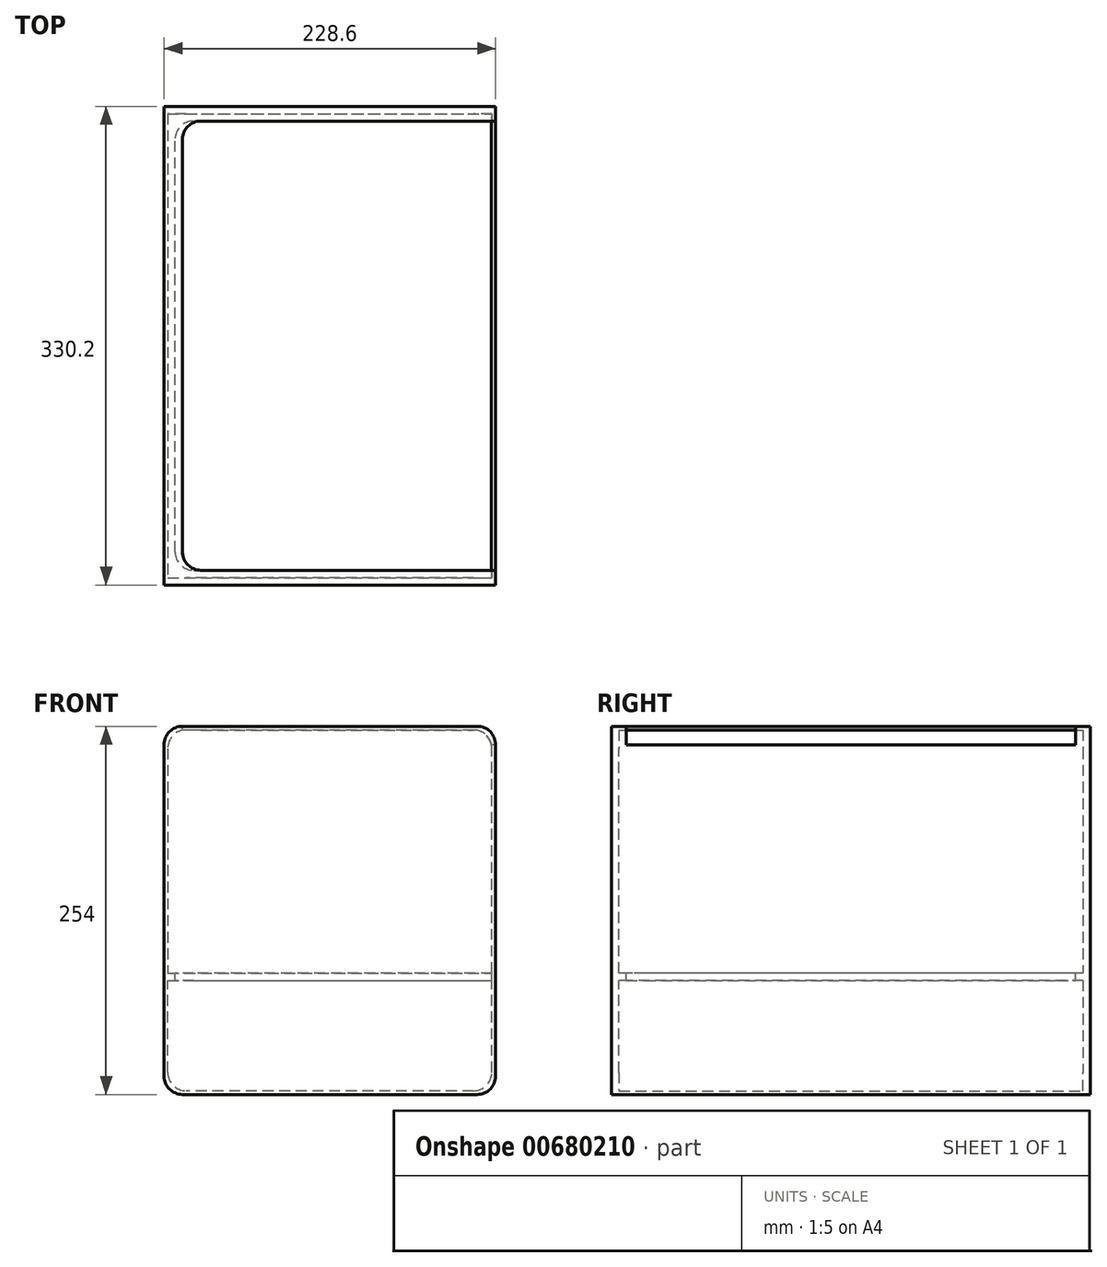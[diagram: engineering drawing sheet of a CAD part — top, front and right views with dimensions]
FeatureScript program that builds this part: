
annotation { "Feature Type Name" : "Feature", "Feature Type Description" : "" }
export const myFeature = defineFeature(function(context is Context, id is Id, definition is map)
    precondition{}
    {
        {
            var Q0;
            Q0=qCreatedBy(makeId("Front.planeOp"),FACE);
            var sketch = newSketch(context, id + "F0", { "sketchPlane" : qUnion([Q0])});
            skLineSegment(sketch, "E0.bottom", {"start": v(101.6, -127) * mm, "end": v(-101.6, -127) * mm});
            skLineSegment(sketch, "E0.top", {"start": v(101.6, 127) * mm, "end": v(-101.6, 127) * mm});
            skLineSegment(sketch, "E0.left", {"start": v(114.3, -114.3) * mm, "end": v(114.3, 114.3) * mm});
            skLineSegment(sketch, "E0.right", {"start": v(-114.3, -114.3) * mm, "end": v(-114.3, 114.3) * mm});
            skPoint(sketch, "E0.middle", {"position": v(0, 0) * mm});
            skPoint(sketch, "E1.visualSharp", {"position": v(114.3, 127) * mm});
            skArc(sketch, "E1.filletArc", {"start": v(114.3, 114.3) * mm, "mid": v(110.58, 123.28) * mm, "end": v(101.6, 127) * mm});
            skPoint(sketch, "E2.visualSharp", {"position": v(-114.3, 127) * mm});
            skArc(sketch, "E2.filletArc", {"start": v(-101.6, 127) * mm, "mid": v(-110.58, 123.28) * mm, "end": v(-114.3, 114.3) * mm});
            skPoint(sketch, "E3.visualSharp", {"position": v(-114.3, -127) * mm});
            skArc(sketch, "E3.filletArc", {"start": v(-114.3, -114.3) * mm, "mid": v(-110.58, -123.28) * mm, "end": v(-101.6, -127) * mm});
            skPoint(sketch, "E4.visualSharp", {"position": v(114.3, -127) * mm});
            skArc(sketch, "E4.filletArc", {"start": v(101.6, -127) * mm, "mid": v(110.58, -123.28) * mm, "end": v(114.3, -114.3) * mm});
            skLineSegment(sketch, "E5.bottom", {"start": v(99.06, -124.46) * mm, "end": v(-99.06, -124.46) * mm});
            skLineSegment(sketch, "E5.top", {"start": v(99.06, 124.46) * mm, "end": v(-99.06, 124.46) * mm});
            skLineSegment(sketch, "E5.left", {"start": v(111.76, -111.76) * mm, "end": v(111.76, 111.76) * mm});
            skLineSegment(sketch, "E5.right", {"start": v(-111.76, -111.76) * mm, "end": v(-111.76, 111.76) * mm});
            skPoint(sketch, "E6.visualSharp", {"position": v(-111.76, 124.46) * mm});
            skArc(sketch, "E6.filletArc", {"start": v(-99.06, 124.46) * mm, "mid": v(-108.04, 120.74) * mm, "end": v(-111.76, 111.76) * mm});
            skPoint(sketch, "E7.visualSharp", {"position": v(111.76, 124.46) * mm});
            skArc(sketch, "E7.filletArc", {"start": v(111.76, 111.76) * mm, "mid": v(108.04, 120.74) * mm, "end": v(99.06, 124.46) * mm});
            skPoint(sketch, "E8.visualSharp", {"position": v(111.76, -124.46) * mm});
            skArc(sketch, "E8.filletArc", {"start": v(99.06, -124.46) * mm, "mid": v(108.04, -120.74) * mm, "end": v(111.76, -111.76) * mm});
            skPoint(sketch, "E9.visualSharp", {"position": v(-111.76, -124.46) * mm});
            skArc(sketch, "E9.filletArc", {"start": v(-111.76, -111.76) * mm, "mid": v(-108.04, -120.74) * mm, "end": v(-99.06, -124.46) * mm});
            skSolve(sketch);
        }
        {
            var Q0;
            Q0 = qSketchRegion(id + "F0", true);
            extrude(context, id + "F1", {"entities" : qUnion([Q0]), "depth" : 165.1 * mm, "offsetDistance" : 25.4 * mm, "hasSecondDirection" : true, "secondDirectionOppositeDirection" : true, "secondDirectionDepth" : 165.1 * mm});
        }
        {
            var Q0;
            Q0=makeQuery(id+"F1.opExtrude","SWEPT_FACE",FACE,{"disambiguationData":[OSD([sQuery(id+"F0.wireOp",EDGE,"E0.top")])]});
            var sketch = newSketch(context, id + "F2", { "sketchPlane" : qUnion([Q0])});
            skLineSegment(sketch, "E10.bottom", {"start": v(312.62, -154.94) * mm, "end": v(-88.9, -154.94) * mm});
            skLineSegment(sketch, "E10.top", {"start": v(312.62, 154.94) * mm, "end": v(-88.9, 154.94) * mm});
            skLineSegment(sketch, "E10.left", {"start": v(312.62, -154.94) * mm, "end": v(312.62, 154.94) * mm});
            skLineSegment(sketch, "E10.right", {"start": v(-101.6, -142.24) * mm, "end": v(-101.6, 142.24) * mm});
            skPoint(sketch, "E10.middle", {"position": v(105.5, 0) * mm});
            skPoint(sketch, "E11.visualSharp", {"position": v(-101.6, -154.94) * mm});
            skArc(sketch, "E11.filletArc", {"start": v(-101.6, -142.24) * mm, "mid": v(-97.88, -151.22) * mm, "end": v(-88.9, -154.94) * mm});
            skPoint(sketch, "E12.visualSharp", {"position": v(-101.6, 154.94) * mm});
            skArc(sketch, "E12.filletArc", {"start": v(-88.9, 154.94) * mm, "mid": v(-97.88, 151.22) * mm, "end": v(-101.6, 142.24) * mm});
            skSolve(sketch);
        }
        {
            var Q0;
            Q0 = qSketchRegion(id + "F2", true);
            extrude(context, id + "F3", {"entities" : qUnion([Q0]), "operationType" : NewBodyOperationType.REMOVE, "oppositeDirection" : true, "depth" : 12.7 * mm, "offsetDistance" : 25.4 * mm});
        }
        {
            var Q0;
            Q0=makeQuery(id+"F1.opExtrude","CAP_FACE",FACE,{"disambiguationData":[OSD([sQuery(id+"F0.wireOp",EDGE,"E0.bottom"),sQuery(id+"F0.wireOp",EDGE,"E0.top"),sQuery(id+"F0.wireOp",EDGE,"E0.left"),sQuery(id+"F0.wireOp",EDGE,"E0.right"),sQuery(id+"F0.wireOp",EDGE,"E1.filletArc"),sQuery(id+"F0.wireOp",EDGE,"E2.filletArc"),sQuery(id+"F0.wireOp",EDGE,"E3.filletArc"),sQuery(id+"F0.wireOp",EDGE,"E4.filletArc"),sQuery(id+"F0.wireOp",EDGE,"E5.bottom"),sQuery(id+"F0.wireOp",EDGE,"E5.top"),sQuery(id+"F0.wireOp",EDGE,"E5.left"),sQuery(id+"F0.wireOp",EDGE,"E5.right"),sQuery(id+"F0.wireOp",EDGE,"E6.filletArc"),sQuery(id+"F0.wireOp",EDGE,"E7.filletArc"),sQuery(id+"F0.wireOp",EDGE,"E8.filletArc"),sQuery(id+"F0.wireOp",EDGE,"E9.filletArc")])],"isStart":true});
            var sketch = newSketch(context, id + "F4", { "sketchPlane" : qUnion([Q0])});
            skLineSegment(sketch, "E13.bottom", {"start": v(101.6, -127) * mm, "end": v(-101.6, -127) * mm});
            skLineSegment(sketch, "E13.top", {"start": v(101.6, 127) * mm, "end": v(-101.6, 127) * mm});
            skLineSegment(sketch, "E13.left", {"start": v(114.3, -114.3) * mm, "end": v(114.3, 114.3) * mm});
            skLineSegment(sketch, "E13.right", {"start": v(-114.3, -114.3) * mm, "end": v(-114.3, 114.3) * mm});
            skPoint(sketch, "E13.middle", {"position": v(0, 0) * mm});
            skPoint(sketch, "E14.visualSharp", {"position": v(114.3, 127) * mm});
            skArc(sketch, "E14.filletArc", {"start": v(114.3, 114.3) * mm, "mid": v(110.58, 123.28) * mm, "end": v(101.6, 127) * mm});
            skPoint(sketch, "E15.visualSharp", {"position": v(-114.3, 127) * mm});
            skArc(sketch, "E15.filletArc", {"start": v(-101.6, 127) * mm, "mid": v(-110.58, 123.28) * mm, "end": v(-114.3, 114.3) * mm});
            skPoint(sketch, "E16.visualSharp", {"position": v(-114.3, -127) * mm});
            skArc(sketch, "E16.filletArc", {"start": v(-114.3, -114.3) * mm, "mid": v(-110.58, -123.28) * mm, "end": v(-101.6, -127) * mm});
            skPoint(sketch, "E17.visualSharp", {"position": v(114.3, -127) * mm});
            skArc(sketch, "E17.filletArc", {"start": v(101.6, -127) * mm, "mid": v(110.58, -123.28) * mm, "end": v(114.3, -114.3) * mm});
            skPoint(sketch, "E18.visualSharp", {"position": v(-111.76, 124.46) * mm});
            skPoint(sketch, "E19.visualSharp", {"position": v(111.76, 124.46) * mm});
            skPoint(sketch, "E20.visualSharp", {"position": v(111.76, -124.46) * mm});
            skPoint(sketch, "E21.visualSharp", {"position": v(-111.76, -124.46) * mm});
            skSolve(sketch);
        }
        {
            var Q0;
            Q0 = qSketchRegion(id + "F4", true);
            extrude(context, id + "F5", {"entities" : qUnion([Q0]), "operationType" : NewBodyOperationType.ADD, "oppositeDirection" : true, "depth" : 5.08 * mm, "offsetDistance" : 25.4 * mm});
        }
        {
            var Q0;
            Q0=makeQuery(id+"F1.opExtrude","CAP_FACE",FACE,{"disambiguationData":[OSD([sQuery(id+"F0.wireOp",EDGE,"E0.bottom"),sQuery(id+"F0.wireOp",EDGE,"E0.top"),sQuery(id+"F0.wireOp",EDGE,"E0.left"),sQuery(id+"F0.wireOp",EDGE,"E0.right"),sQuery(id+"F0.wireOp",EDGE,"E1.filletArc"),sQuery(id+"F0.wireOp",EDGE,"E2.filletArc"),sQuery(id+"F0.wireOp",EDGE,"E3.filletArc"),sQuery(id+"F0.wireOp",EDGE,"E4.filletArc"),sQuery(id+"F0.wireOp",EDGE,"E5.bottom"),sQuery(id+"F0.wireOp",EDGE,"E5.top"),sQuery(id+"F0.wireOp",EDGE,"E5.left"),sQuery(id+"F0.wireOp",EDGE,"E5.right"),sQuery(id+"F0.wireOp",EDGE,"E6.filletArc"),sQuery(id+"F0.wireOp",EDGE,"E7.filletArc"),sQuery(id+"F0.wireOp",EDGE,"E8.filletArc"),sQuery(id+"F0.wireOp",EDGE,"E9.filletArc")])],"isStart":false});
            var sketch = newSketch(context, id + "F6", { "sketchPlane" : qUnion([Q0])});
            skLineSegment(sketch, "E22.bottom", {"start": v(101.6, -127) * mm, "end": v(-101.6, -127) * mm});
            skLineSegment(sketch, "E22.top", {"start": v(101.6, 127) * mm, "end": v(-101.6, 127) * mm});
            skLineSegment(sketch, "E22.left", {"start": v(114.3, -114.3) * mm, "end": v(114.3, 114.3) * mm});
            skLineSegment(sketch, "E22.right", {"start": v(-114.3, -114.3) * mm, "end": v(-114.3, 114.3) * mm});
            skPoint(sketch, "E22.middle", {"position": v(0, 0) * mm});
            skPoint(sketch, "E23.visualSharp", {"position": v(114.3, 127) * mm});
            skArc(sketch, "E23.filletArc", {"start": v(114.3, 114.3) * mm, "mid": v(110.58, 123.28) * mm, "end": v(101.6, 127) * mm});
            skPoint(sketch, "E24.visualSharp", {"position": v(-114.3, 127) * mm});
            skArc(sketch, "E24.filletArc", {"start": v(-101.6, 127) * mm, "mid": v(-110.58, 123.28) * mm, "end": v(-114.3, 114.3) * mm});
            skPoint(sketch, "E25.visualSharp", {"position": v(-114.3, -127) * mm});
            skArc(sketch, "E25.filletArc", {"start": v(-114.3, -114.3) * mm, "mid": v(-110.58, -123.28) * mm, "end": v(-101.6, -127) * mm});
            skPoint(sketch, "E26.visualSharp", {"position": v(114.3, -127) * mm});
            skArc(sketch, "E26.filletArc", {"start": v(101.6, -127) * mm, "mid": v(110.58, -123.28) * mm, "end": v(114.3, -114.3) * mm});
            skPoint(sketch, "E27.visualSharp", {"position": v(-111.76, 124.46) * mm});
            skPoint(sketch, "E28.visualSharp", {"position": v(111.76, 124.46) * mm});
            skPoint(sketch, "E29.visualSharp", {"position": v(111.76, -124.46) * mm});
            skPoint(sketch, "E30.visualSharp", {"position": v(-111.76, -124.46) * mm});
            skSolve(sketch);
        }
        {
            var Q0;
            Q0 = qSketchRegion(id + "F6", true);
            extrude(context, id + "F7", {"entities" : qUnion([Q0]), "operationType" : NewBodyOperationType.ADD, "oppositeDirection" : true, "depth" : 5.08 * mm, "offsetDistance" : 25.4 * mm});
        }
        {
            var Q0;
            Q0=makeQuery(id+"F7.opExtrude","CAP_FACE",FACE,{"disambiguationData":[OSD([sQuery(id+"F6.wireOp",EDGE,"E22.bottom"),sQuery(id+"F6.wireOp",EDGE,"E22.top"),sQuery(id+"F6.wireOp",EDGE,"E22.left"),sQuery(id+"F6.wireOp",EDGE,"E22.right"),sQuery(id+"F6.wireOp",EDGE,"E23.filletArc"),sQuery(id+"F6.wireOp",EDGE,"E24.filletArc"),sQuery(id+"F6.wireOp",EDGE,"E25.filletArc"),sQuery(id+"F6.wireOp",EDGE,"E26.filletArc")])],"isStart":false});
            var sketch = newSketch(context, id + "F8", { "sketchPlane" : qUnion([Q0])});
            skLineSegment(sketch, "E31.bottom", {"start": v(111.76, -43.18) * mm, "end": v(-111.76, -43.18) * mm});
            skLineSegment(sketch, "E31.top", {"start": v(111.76, -48.26) * mm, "end": v(-111.76, -48.26) * mm});
            skLineSegment(sketch, "E31.left", {"start": v(111.76, -43.18) * mm, "end": v(111.76, -48.26) * mm});
            skLineSegment(sketch, "E31.right", {"start": v(-111.76, -43.18) * mm, "end": v(-111.76, -48.26) * mm});
            skSolve(sketch);
        }
        {
            var Q0;
            Q0 = qSketchRegion(id + "F8", true);
            extrude(context, id + "F9", {"entities" : qUnion([Q0]), "operationType" : NewBodyOperationType.ADD, "depth" : 320.04 * mm, "offsetDistance" : 25.4 * mm});
        }
        {
            var Q0;
            Q0=makeQuery(id+"F9.opExtrude","SWEPT_FACE",FACE,{"disambiguationData":[OSD([sQuery(id+"F8.wireOp",EDGE,"E31.bottom")])]});
            var sketch = newSketch(context, id + "F10", { "sketchPlane" : qUnion([Q0])});
            skLineSegment(sketch, "E32.bottom", {"start": v(111.76, 154.94) * mm, "end": v(-93.98, 154.94) * mm});
            skLineSegment(sketch, "E32.top", {"start": v(111.76, -154.94) * mm, "end": v(-93.98, -154.94) * mm});
            skLineSegment(sketch, "E32.left", {"start": v(111.76, 154.94) * mm, "end": v(111.76, -154.94) * mm});
            skLineSegment(sketch, "E32.right", {"start": v(-106.68, 142.24) * mm, "end": v(-106.68, -142.24) * mm});
            skPoint(sketch, "E33.visualSharp", {"position": v(-106.68, -154.94) * mm});
            skArc(sketch, "E33.filletArc", {"start": v(-106.68, -142.24) * mm, "mid": v(-102.96, -151.22) * mm, "end": v(-93.98, -154.94) * mm});
            skPoint(sketch, "E34.visualSharp", {"position": v(-106.68, 154.94) * mm});
            skArc(sketch, "E34.filletArc", {"start": v(-93.98, 154.94) * mm, "mid": v(-102.96, 151.22) * mm, "end": v(-106.68, 142.24) * mm});
            skSolve(sketch);
        }
        {
            var Q0;
            Q0 = qSketchRegion(id + "F10", true);
            extrude(context, id + "F11", {"entities" : qUnion([Q0]), "operationType" : NewBodyOperationType.REMOVE, "oppositeDirection" : true, "depth" : 25.4 * mm, "offsetDistance" : 25.4 * mm});
        }
    });
